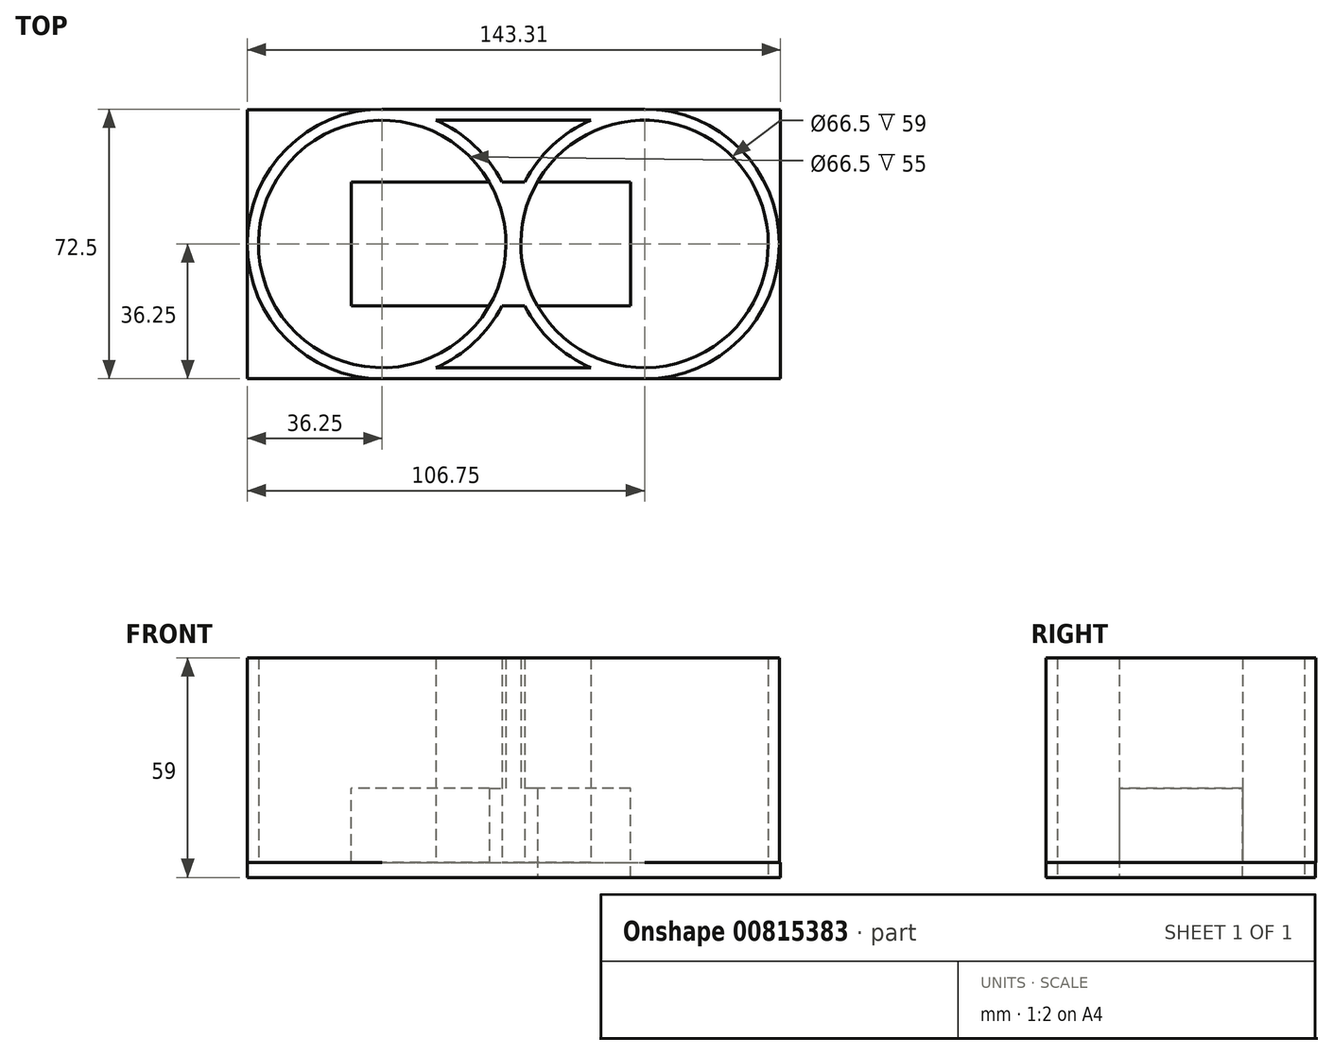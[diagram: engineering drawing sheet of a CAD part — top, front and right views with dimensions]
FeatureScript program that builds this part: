
annotation { "Feature Type Name" : "Feature", "Feature Type Description" : "" }
export const myFeature = defineFeature(function(context is Context, id is Id, definition is map)
    precondition{}
    {
        {
            var Q0;
            Q0=qCreatedBy(makeId("Top.planeOp"),FACE);
            var sketch = newSketch(context, id + "F0", { "sketchPlane" : qUnion([Q0])});
            skArc(sketch, "E0", {"start": v(33.25, 33.25) * mm, "mid": v(0, 0) * mm, "end": v(33.25, -33.25) * mm});
            skPoint(sketch, "E1.orphan", {"position": v(137, 0) * mm});
            skArc(sketch, "E2", {"start": v(103.75, -33.25) * mm, "mid": v(137, 0) * mm, "end": v(103.75, 33.25) * mm});
            skLineSegment(sketch, "E3", {"start": v(47.69, 33.25) * mm, "end": v(89.31, 33.25) * mm});
            skLineSegment(sketch, "E4", {"start": v(47.69, -33.25) * mm, "end": v(89.31, -33.25) * mm});
            skPoint(sketch, "E5.start.orphan", {"position": v(0, 0) * mm});
            skArc(sketch, "E6.0", {"start": v(103.75, -36.25) * mm, "mid": v(140, 0) * mm, "end": v(103.75, 36.25) * mm});
            skLineSegment(sketch, "E6.1", {"start": v(33.25, -36.25) * mm, "end": v(103.75, -36.25) * mm});
            skArc(sketch, "E6.2", {"start": v(33.25, 36.25) * mm, "mid": v(-3, 0) * mm, "end": v(33.25, -36.25) * mm});
            skLineSegment(sketch, "E6.3", {"start": v(33.25, 36.25) * mm, "end": v(103.75, 36.25) * mm});
            skCircle(sketch, "E7", {"center": v(33.25, 0) * mm, "radius": 33.25 * mm});
            skCircle(sketch, "E8", {"center": v(103.75, 0) * mm, "radius": 33.25 * mm});
            skArc(sketch, "E9", {"start": v(65.46, 16.63) * mm, "mid": v(-3, 0) * mm, "end": v(65.46, -16.63) * mm});
            skArc(sketch, "E10", {"start": v(71.54, -16.63) * mm, "mid": v(140, 0) * mm, "end": v(71.54, 16.63) * mm});
            skLineSegment(sketch, "E11", {"start": v(65.46, 16.62) * mm, "end": v(71.54, 16.62) * mm});
            skLineSegment(sketch, "E12", {"start": v(65.46, -16.63) * mm, "end": v(72.4, -16.63) * mm});
            skPoint(sketch, "E13.startSnap0", {"position": v(66.95, 16.62) * mm});
            skLineSegment(sketch, "E14", {"start": v(72.4, -16.63) * mm, "end": v(71.54, -16.63) * mm});
            skPoint(sketch, "E15.end.orphan", {"position": v(33.25, -16.62) * mm});
            skPoint(sketch, "E16.start.orphan", {"position": v(33.25, 16.62) * mm});
            skPoint(sketch, "E17.orphan", {"position": v(111.56, -16.63) * mm});
            skPoint(sketch, "E18.orphan", {"position": v(100.64, 16.62) * mm});
            skPoint(sketch, "E19.orphan", {"position": v(62.05, 16.62) * mm});
            skLineSegment(sketch, "E20", {"start": v(33.25, -16.62) * mm, "end": v(33.25, 16.62) * mm});
            skSolve(sketch);
        }
        {
            var Q0;
            Q0=qCreatedBy(makeId("Right.planeOp"),FACE);
            var sketch = newSketch(context, id + "F1", { "sketchPlane" : qUnion([Q0])});
            skLineSegment(sketch, "E21", {"start": v(0, 0) * mm, "end": v(-33.25, 0) * mm});
            skLineSegment(sketch, "E22.bottom", {"start": v(-16.62, 0) * mm, "end": v(16.63, 0) * mm});
            skLineSegment(sketch, "E22.top", {"start": v(-16.63, 20) * mm, "end": v(16.62, 20) * mm});
            skLineSegment(sketch, "E22.left", {"start": v(-16.62, 0) * mm, "end": v(-16.62, 20) * mm});
            skLineSegment(sketch, "E22.right", {"start": v(16.63, 0) * mm, "end": v(16.62, 20) * mm});
            skSolve(sketch);
        }
        {
            var Q0;
            Q0=makeQuery(id+"F1.imprint","IMPRINT",FACE,{"disambiguationData":[TD([[makeQuery(id+"F1.imprint","IMPRINT",EDGE,{"derivedFrom":sQuery(id+"F1.wireOp",EDGE,"E22.top")}),-1.0]])]});
            extrude(context, id + "F2", {"entities" : qUnion([Q0]), "depth" : 100 * mm, "offsetDistance" : 25 * mm, "hasSecondDirection" : true, "secondDirectionOppositeDirection" : true, "secondDirectionDepth" : -25 * mm});
        }
        {
            var Q0;
            Q0 = qSketchRegion(id + "F0", true);
            extrude(context, id + "F3", {"entities" : qUnion([Q0]), "operationType" : NewBodyOperationType.ADD, "depth" : 55 * mm, "offsetDistance" : 25 * mm});
        }
        {
            var Q0;
            Q0=makeQuery(id+"F3.boolean.opBoolean","MERGE",FACE,{"derivedFrom":[makeQuery(id+"F2.opExtrude","SWEPT_FACE",FACE,{"disambiguationData":[OSD([sQuery(id+"F1.wireOp",EDGE,"E22.bottom")])]}),makeQuery(id+"F3.opExtrude","CAP_FACE",FACE,{"disambiguationData":[OSD([sQuery(id+"F0.wireOp",EDGE,"E3"),sQuery(id+"F0.wireOp",EDGE,"E4"),sQuery(id+"F0.wireOp",EDGE,"E6.1"),sQuery(id+"F0.wireOp",EDGE,"E6.3"),sQuery(id+"F0.wireOp",EDGE,"E7"),sQuery(id+"F0.wireOp",EDGE,"E8"),sQuery(id+"F0.wireOp",EDGE,"E9"),sQuery(id+"F0.wireOp",EDGE,"E10"),sQuery(id+"F0.wireOp",EDGE,"E12"),sQuery(id+"F0.wireOp",EDGE,"E11")])],"isStart":true})]});
            var sketch = newSketch(context, id + "F4", { "sketchPlane" : qUnion([Q0])});
            skPoint(sketch, "E23.firstSnap0", {"position": v(-3, 0) * mm});
            skLineSegment(sketch, "E23.bottom", {"start": v(-3, 36.25) * mm, "end": v(140.3, 36.25) * mm});
            skLineSegment(sketch, "E23.top", {"start": v(-3, -36.1) * mm, "end": v(140.3, -36.1) * mm});
            skLineSegment(sketch, "E23.left", {"start": v(-3, 36.25) * mm, "end": v(-3, -36.1) * mm});
            skLineSegment(sketch, "E23.right", {"start": v(140.3, 36.25) * mm, "end": v(140.3, -36.1) * mm});
            skSolve(sketch);
        }
        {
            var Q0;
            {var subQ20=sQuery(id+"F1.wireOp",EDGE,"E22.bottom");Q0=makeQuery(id+"F4.imprint","IMPRINT",FACE,{"disambiguationData":[TD([[makeQuery(id+"F4.imprint","IMPRINT",EDGE,{"derivedFrom":makeQuery(id+"F2.opExtrude","CAP_EDGE",EDGE,{"disambiguationData":[OSD([subQ20])],"isStart":true})}),1.0]])]});}
            var Q1;
            {var subQ0=sQuery(id+"F4.wireOp",EDGE,"E23.bottom");var subQ4=sQuery(id+"F4.wireOp",EDGE,"E23.left");var subQ5=makeQuery(id+"F4.imprint","INTERSECT",VERTEX,{"derivedFrom":[subQ0,subQ4]});Q1=makeQuery(id+"F4.imprint","IMPRINT",FACE,{"disambiguationData":[TD([[makeQuery(id+"F4.imprint","IMPRINT",EDGE,{"disambiguationData":[TD([[subQ5,-1.0]])],"derivedFrom":subQ0}),-1.0]])]});}
            var Q2;
            {var subQ4=sQuery(id+"F4.wireOp",EDGE,"E23.right");Q2=makeQuery(id+"F4.imprint","IMPRINT",FACE,{"disambiguationData":[TD([[makeQuery(id+"F4.imprint","IMPRINT",EDGE,{"derivedFrom":subQ4}),-1.0]])]});}
            var Q3;
            {var subQ0=sQuery(id+"F0.wireOp",EDGE,"E4");Q3=makeQuery(id+"F4.imprint","IMPRINT",FACE,{"disambiguationData":[TD([[makeQuery(id+"F4.imprint","IMPRINT",EDGE,{"derivedFrom":makeQuery(id+"F3.opExtrude","CAP_EDGE",EDGE,{"disambiguationData":[OSD([subQ0])],"isStart":true})}),-1.0]])]});}
            var Q4;
            {var subQ0=sQuery(id+"F1.wireOp",EDGE,"E22.bottom");Q4=makeQuery(id+"F4.imprint","IMPRINT",FACE,{"disambiguationData":[TD([[makeQuery(id+"F4.imprint","IMPRINT",EDGE,{"derivedFrom":makeQuery(id+"F2.opExtrude","CAP_EDGE",EDGE,{"disambiguationData":[OSD([subQ0])],"isStart":true})}),-1.0]])]});}
            var Q5;
            {var subQ0=sQuery(id+"F1.wireOp",EDGE,"E22.bottom");Q5=makeQuery(id+"F4.imprint","IMPRINT",FACE,{"disambiguationData":[TD([[makeQuery(id+"F4.imprint","IMPRINT",EDGE,{"derivedFrom":makeQuery(id+"F2.opExtrude","CAP_EDGE",EDGE,{"disambiguationData":[OSD([subQ0])],"isStart":false})}),1.0]])]});}
            var Q6;
            {var subQ0=sQuery(id+"F0.wireOp",EDGE,"E3");Q6=makeQuery(id+"F4.imprint","IMPRINT",FACE,{"disambiguationData":[TD([[makeQuery(id+"F4.imprint","IMPRINT",EDGE,{"derivedFrom":makeQuery(id+"F3.opExtrude","CAP_EDGE",EDGE,{"disambiguationData":[OSD([subQ0])],"isStart":true})}),1.0]])]});}
            var Q7;
            {var subQ0=sQuery(id+"F4.wireOp",EDGE,"E23.left");var subQ1=sQuery(id+"F4.wireOp",EDGE,"E23.top");var subQ2=makeQuery(id+"F4.imprint","INTERSECT",VERTEX,{"derivedFrom":[subQ1,subQ0]});Q7=makeQuery(id+"F4.imprint","IMPRINT",FACE,{"disambiguationData":[TD([[makeQuery(id+"F4.imprint","IMPRINT",EDGE,{"disambiguationData":[TD([[subQ2,-1.0]])],"derivedFrom":subQ1}),1.0]])]});}
            extrude(context, id + "F5", {"entities" : qUnion([Q0, Q1, Q2, Q3, Q4, Q5, Q6, Q7]), "operationType" : NewBodyOperationType.ADD, "depth" : 4 * mm, "offsetDistance" : 25 * mm});
        }
    });
